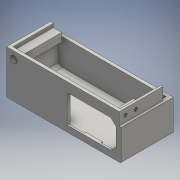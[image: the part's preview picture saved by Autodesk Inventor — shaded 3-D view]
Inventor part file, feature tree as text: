
AUTODESK INVENTOR PART (.ipt)
format: ipt  version: 2016 (Build 200138000, 138)  size: 649,728 bytes
history: native  units: mm
features: extrude x6, sketch x6, projected_geometry x5, other x2, fillet x2
ambient origin geometry x8: Origin, YZ Plane, XZ Plane, XY Plane, X Axis, Y Axis, Z Axis, Center Point
bodies: Solid1 (feature_tree)
feature tree (21):
  other  "psu_cover_20a_i3_steel"
  other  "MeshFeature1"
  extrude  "Extrusion1"  Depth=10.0mm TaperAngle=0.0deg
  extrude  "Extrusion2"  Depth=27.0mm
  extrude  "Extrusion3"  Depth=6.0mm
  extrude  "Extrusion4"  Depth=5.0mm
  extrude  "Extrusion5"  Depth=5.0mm
  fillet  "Fillet1"  Radius=10.0mm
  fillet  "Fillet2"  Radius=10.0mm
  extrude  "Extrusion6"  Depth=10.0mm TaperAngle=0.0deg
  sketch  "Sketch1"  dims[d0=10.0mm d1=0.0mm d2=10.0mm d3=0.0mm]
  projected_geometry  "Projected Loop1"
  sketch  "Sketch2"  dims[d4=47.0mm d5=27.0mm]
  projected_geometry  "Projected Loop2"
  sketch  "Sketch3"  dims[d6=5.0mm d7=6.0mm]
  sketch  "Sketch4"  dims[d8=5.0mm d9=5.0mm]
  projected_geometry  "Projected Loop3"
  sketch  "Sketch5"  dims[d10=5.0mm d11=5.0mm d12=10.0mm d13=0.0mm d14=10.0mm d15=0.0mm]
  projected_geometry  "Projected Loop4"
  sketch  "Sketch6"  dims[d16=14.0mm d17=10.0mm d18=0.0mm d19=3.0mm d20=1.0mm d21=1.5mm d22=15.0mm d23=15.0mm d24=11.0mm d25=11.0mm d26=1.5mm d27=0.0mm]
  projected_geometry  "Projected Loop5"
